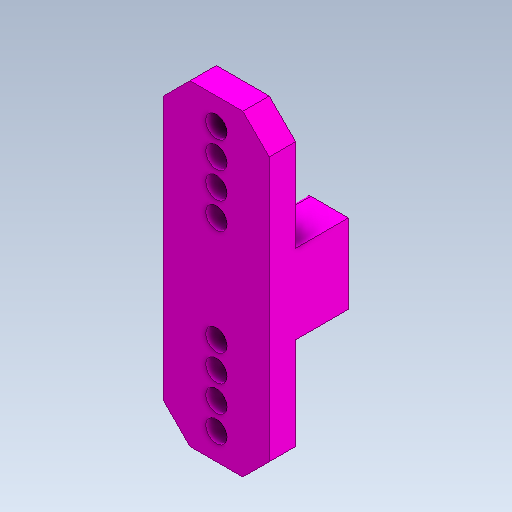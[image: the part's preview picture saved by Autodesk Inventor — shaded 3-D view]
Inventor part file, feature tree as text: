
AUTODESK INVENTOR PART (.ipt)
format: ipt  version: 2020 (Build 240168000, 168)  size: 136,704 bytes
history: native  units: in
note: dims shown in document units (in); Inventor stores cm internally (conversion verified against a paired STEP export)
features: other x3, sketch x3
ambient origin geometry x8: Origin, YZ Plane, XZ Plane, XY Plane, X Axis, Y Axis, Z Axis, Center Point
bodies: Solid1 (feature_tree)
feature tree (6):
  other  "ShaftRest.ipt"
  other  "Solid1::ShaftRest.ipt"
  other  "TaggingFeature1"
  sketch  "Sketch1"  dims[d0=0.3937in]
  sketch  "Sketch2"
  sketch  "Sketch3"
